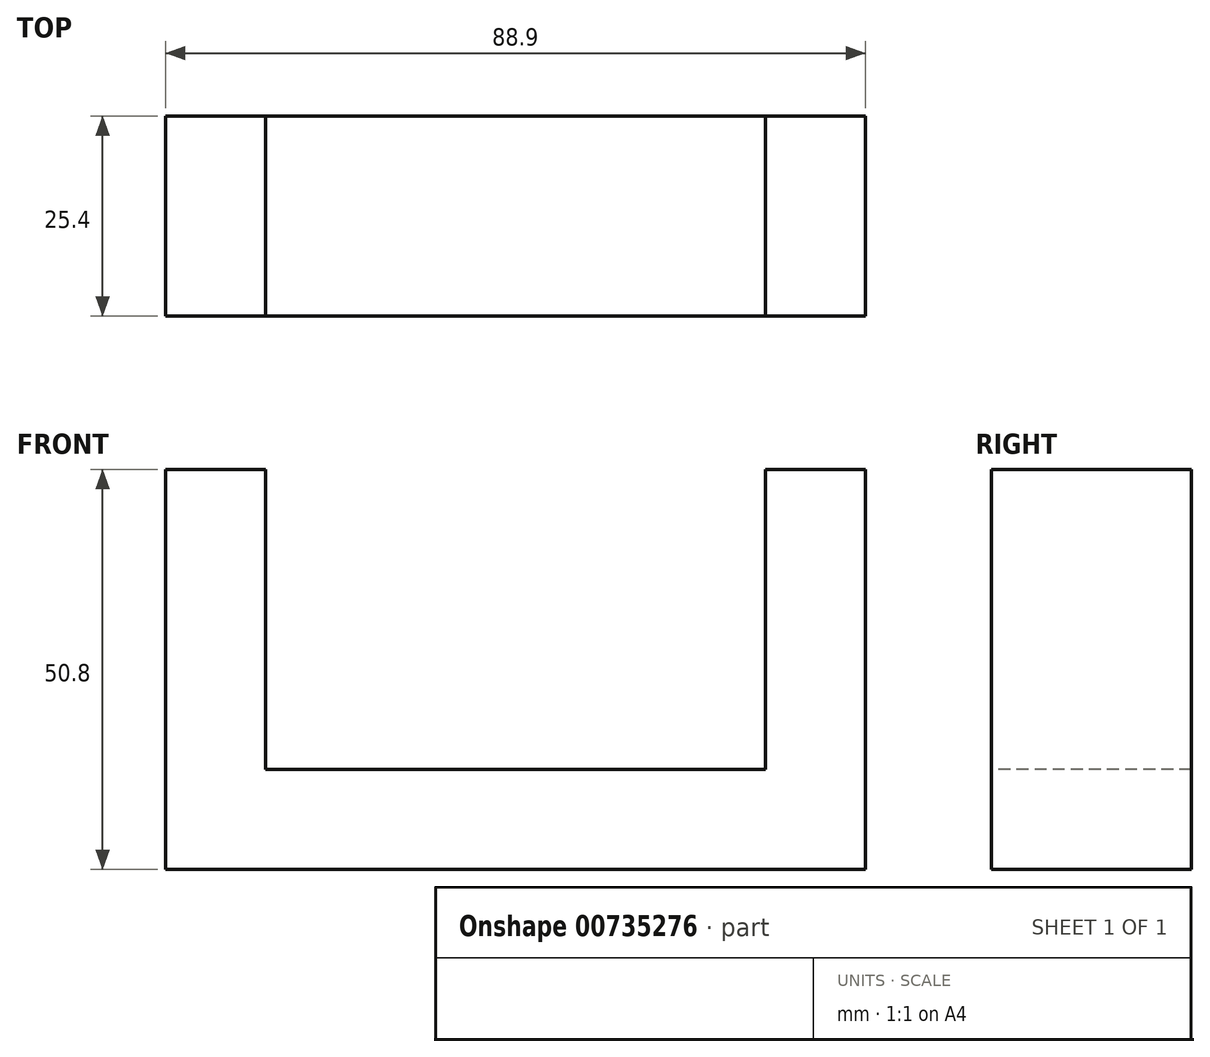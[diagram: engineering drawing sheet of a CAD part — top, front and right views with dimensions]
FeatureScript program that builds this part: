
annotation { "Feature Type Name" : "Feature", "Feature Type Description" : "" }
export const myFeature = defineFeature(function(context is Context, id is Id, definition is map)
    precondition{}
    {
        {
            var Q0;
            Q0=qCreatedBy(makeId("Front.planeOp"),FACE);
            var sketch = newSketch(context, id + "F0", { "sketchPlane" : qUnion([Q0])});
            skLineSegment(sketch, "E0", {"start": v(-65, 38.1) * mm, "end": v(-65, -12.7) * mm});
            skLineSegment(sketch, "E1", {"start": v(-65, -12.7) * mm, "end": v(23.9, -12.7) * mm});
            skLineSegment(sketch, "E2", {"start": v(23.9, -12.7) * mm, "end": v(23.9, 38.1) * mm});
            skLineSegment(sketch, "E3", {"start": v(23.9, 38.1) * mm, "end": v(11.2, 38.1) * mm});
            skLineSegment(sketch, "E4", {"start": v(-65, 38.1) * mm, "end": v(-52.3, 38.1) * mm});
            skLineSegment(sketch, "E5", {"start": v(-52.3, 38.1) * mm, "end": v(-52.3, 0) * mm});
            skLineSegment(sketch, "E6", {"start": v(-52.3, 0) * mm, "end": v(11.2, 0) * mm});
            skLineSegment(sketch, "E7", {"start": v(11.2, 0) * mm, "end": v(11.2, 38.1) * mm});
            skSolve(sketch);
        }
        {
            var Q0;
            Q0 = qSketchRegion(id + "F0", true);
            extrude(context, id + "F1", {"entities" : qUnion([Q0]), "oppositeDirection" : true, "depth" : 25.4 * mm, "offsetDistance" : 25.4 * mm});
        }
    });
